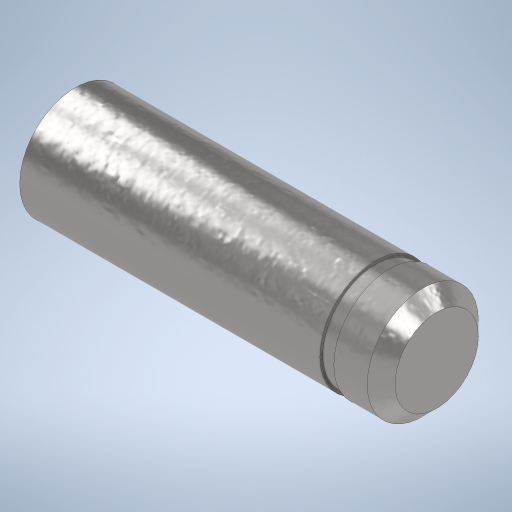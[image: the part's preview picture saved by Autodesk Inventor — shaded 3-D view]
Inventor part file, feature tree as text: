
AUTODESK INVENTOR PART (.ipt)
format: ipt  version: 2024 (Build 280153000, 153)  size: 306,688 bytes
history: native  units: mm
features: revolve x1, chamfer x1, sketch x1
ambient origin geometry x8: Origin, YZ Plane, XZ Plane, XY Plane, X Axis, Y Axis, Z Axis, Center Point
bodies: Volumenkörper1 (feature_tree)
feature tree (3):
  revolve  "Umdrehung1"
  chamfer  "Fasen1"  Distance=0.5mm
  sketch  "Skizze1"  dims[d0=13.0mm d1=0.5mm d2=10.8mm d4=3.8mm d5=4.0mm d6=90.0deg d7=0.5mm d8=2.0mm d9=45.0deg]
